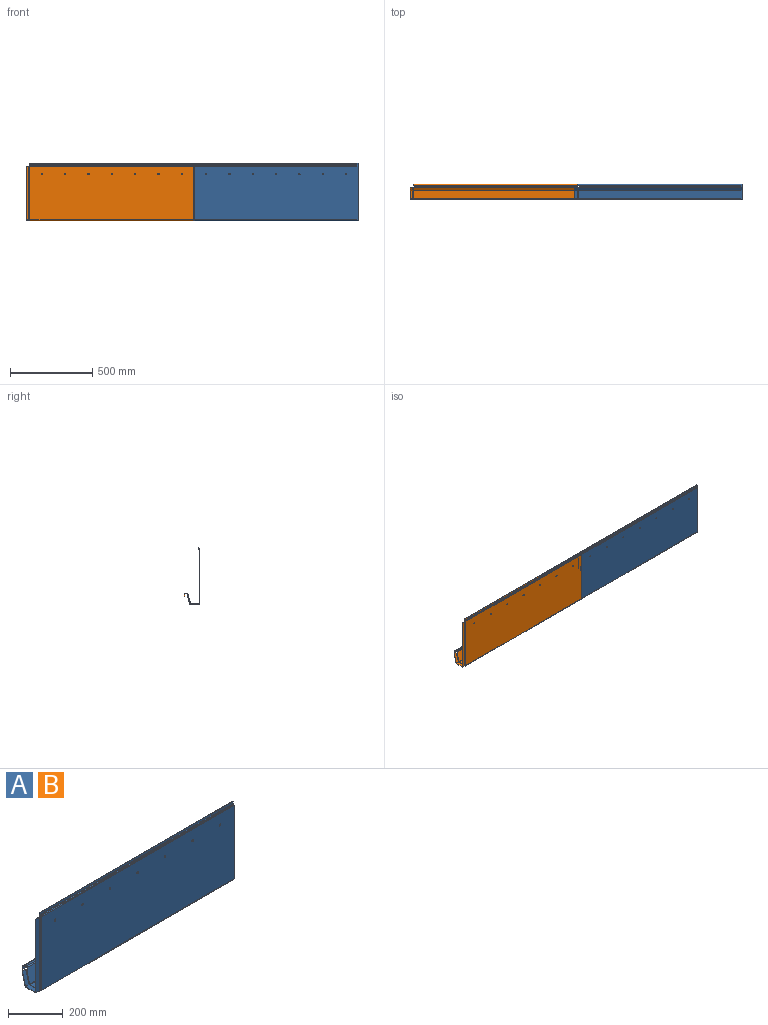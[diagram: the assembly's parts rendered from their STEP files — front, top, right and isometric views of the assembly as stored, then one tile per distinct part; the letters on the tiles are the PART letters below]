
ASSEMBLY  parts=2 mates=1
PART A: 122 faces, bbox 1022x95.1x350 mm
  f0: plane 327.93x2mm, normal (1,0,0), area 655.9mm2, adj f8,f9,f42,f51
  f1: cylinder r=4mm len=8mm, axis (0,1,0), area 50.3mm2, adj f8,f9
  f2: cylinder r=4mm len=8mm, axis (0,1,0), area 50.3mm2, adj f8,f9
  f3: cylinder r=4mm len=8mm, axis (0,1,0), area 50.3mm2, adj f8,f9
  f4: cylinder r=4mm len=8mm, axis (0,1,0), area 50.3mm2, adj f8,f9
  f5: cylinder r=4mm len=8mm, axis (0,1,0), area 50.3mm2, adj f8,f9
  f6: cylinder r=4mm len=8mm, axis (0,1,0), area 50.3mm2, adj f8,f9
  f7: cylinder r=4mm len=8mm, axis (0,1,0), area 50.3mm2, adj f8,f9
  f8: plane 997.93x327.93mm, normal (0,1,0), area 326897.8mm2, adj f0,f1,f2,f3,f4,f5,f6,f7
  f9: plane 997.93x327.93mm, normal (0,-1,0), area 326897.8mm2, adj f0,f1,f2,f3,f4,f5,f6,f7
  f10: cylinder r=2.5mm len=2mm, axis (0,-1,0), area 1.3mm2, adj f8,f9,f52,f91
  f11: plane 62.2x18.46mm, normal (1,0,0), area 127.7mm2, adj f12,f13,f16,f34
  f12: plane 997.93x61.69mm, normal (0,-0.97,0.26), area 63697.8mm2, adj f11,f14,f15,f18,f37,f115
  f13: plane 997.93x61.69mm, normal (0,0.97,-0.26), area 63697.8mm2, adj f11,f14,f15,f19,f36,f114
  f14: cylinder r=4.47mm len=2.36mm, axis (0,0.97,-0.26), area 5.5mm2, adj f12,f13,f35,f112
  f15: cylinder r=8.8mm len=6.89mm, axis (0,0.97,-0.26), area 19.4mm2, adj f12,f13,f17,f113
  f16: plane 4.83x4.22mm, normal (1,0,0), area 10.5mm2, adj f11,f18,f19,f21
  f17: bspline ~4.83x4.22mm, area 10.6mm2, adj f15,f18,f19,f24
  f18: cylinder r=5mm len=991.04mm, axis (1,0,0), area 6486.3mm2, adj f12,f16,f17,f22
  f19: cylinder r=3mm len=991.04mm, axis (1,0,0), area 3891.8mm2, adj f13,f16,f17,f23
  f20: plane 3.47x2mm, normal (-1,0,0), area 6.9mm2, adj f22,f23,f24,f26
  f21: plane 9.7x2mm, normal (1,0,0), area 19.4mm2, adj f16,f22,f23,f25
  f22: plane 1000x9.7mm, normal (0,0,1), area 9656mm2, adj f18,f20,f21,f24,f27
  f23: plane 1000x9.7mm, normal (0,0,-1), area 9656mm2, adj f19,f20,f21,f24,f28
  f24: cylinder r=8.8mm len=8.96mm, axis (0,0,-1), area 23.5mm2, adj f17,f20,f22,f23
  f25: plane 5x5mm, normal (1,0,0), area 12.6mm2, adj f21,f27,f28,f30
  f26: plane 5x5mm, normal (-1,0,0), area 12.6mm2, adj f20,f27,f28,f29
  f27: cylinder r=5mm len=1000mm, axis (1,0,0), area 7854mm2, adj f22,f25,f26,f32
  f28: cylinder r=3mm len=1000mm, axis (1,0,0), area 4712.4mm2, adj f23,f25,f26,f33
  f29: plane 12x2mm, normal (-1,0,0), area 24mm2, adj f26,f31,f32,f33
  f30: plane 12x2mm, normal (1,0,0), area 24mm2, adj f25,f31,f32,f33
  f31: plane 1000x2mm, normal (0,0,-1), area 2000mm2, adj f29,f30,f32,f33
  f32: plane 1000x12mm, normal (0,1,0), area 12000mm2, adj f27,f29,f30,f31
  f33: plane 1000x12mm, normal (0,-1,0), area 12000mm2, adj f28,f29,f30,f31
  f34: plane 4.83x4.22mm, normal (1,0,0), area 10.5mm2, adj f11,f36,f37,f38
  f35: bspline ~4.83x4.22mm, area 11.1mm2, adj f14,f36,f37,f41
  f36: cylinder r=5mm len=995.8mm, axis (1,0,0), area 6513.9mm2, adj f13,f34,f35,f40
  f37: cylinder r=3mm len=995.8mm, axis (1,0,0), area 3908.3mm2, adj f12,f34,f35,f39
  f38: plane 51.16x2mm, normal (1,0,0), area 102.3mm2, adj f34,f39,f40,f42
  f39: plane 997.93x51.16mm, normal (0,0,1), area 51055.3mm2, adj f37,f38,f41,f45,f83
  f40: plane 997.93x51.16mm, normal (0,0,-1), area 51055.3mm2, adj f36,f38,f41,f44,f82
  f41: cylinder r=4.47mm len=2.13mm, axis (0,0,-1), area 5.5mm2, adj f35,f39,f40,f81
  f42: plane 5x5mm, normal (1,0,0), area 12.6mm2, adj f0,f38,f44,f45
  f43: plane 5x5mm, normal (-1,0,0), area 12.6mm2, adj f44,f45,f80,f90
  f44: cylinder r=5mm len=997.93mm, axis (1,0,0), area 7837.7mm2, adj f9,f40,f42,f43
  f45: cylinder r=3mm len=997.93mm, axis (1,0,0), area 4702.6mm2, adj f8,f39,f42,f43
  f46: plane 3.43x3.43mm, normal (-1,0,0), area 5.7mm2, adj f48,f49,f50,f56
  f47: plane 4.07x4.07mm, normal (1,0,0), area 7.5mm2, adj f48,f49,f51,f55
  f48: plane 1000x2.66mm, normal (0,0.71,-0.71), area 3755.5mm2, adj f46,f47,f50,f54,f57
  f49: plane 1000x2.66mm, normal (0,-0.71,0.71), area 3755.5mm2, adj f46,f47,f50,f53,f58
  f50: cylinder r=2.5mm len=2.52mm, axis (0,-0.71,0.71), area 5.6mm2, adj f46,f48,f49,f52
  f51: plane 3.54x2.88mm, normal (1,0,0), area 6.3mm2, adj f0,f47,f53,f54
  f52: bspline ~3.54x2.88mm, area 6.7mm2, adj f10,f50,f53,f54
  f53: cylinder r=5mm len=997.48mm, axis (1,0,0), area 3915.7mm2, adj f9,f49,f51,f52
  f54: cylinder r=3mm len=997.48mm, axis (1,0,0), area 2349.4mm2, adj f8,f48,f51,f52
  f55: plane 3.54x2.88mm, normal (1,0,0), area 6.3mm2, adj f47,f57,f58,f61
  f56: plane 3.54x2.88mm, normal (-1,0,0), area 6.3mm2, adj f46,f57,f58,f59
  f57: cylinder r=5mm len=1000mm, axis (1,0,0), area 3927mm2, adj f48,f55,f56,f62
  f58: cylinder r=3mm len=1000mm, axis (1,0,0), area 2356.2mm2, adj f49,f55,f56,f63
  f59: plane 8.76x2mm, normal (-1,0,0), area 17.5mm2, adj f56,f60,f62,f63
  f60: plane 1000x2mm, normal (0,0,1), area 2000mm2, adj f59,f61,f62,f63
  f61: plane 8.76x2mm, normal (1,0,0), area 17.5mm2, adj f55,f60,f62,f63
  f62: plane 1000x8.76mm, normal (0,1,0), area 8757.4mm2, adj f57,f59,f60,f61
  f63: plane 1000x8.76mm, normal (0,-1,0), area 8757.4mm2, adj f58,f59,f60,f61
  f64: plane 2.04x1.41mm, normal (0.71,0,-0.71), area 4.1mm2, adj f66,f67,f68,f80
  f65: plane 1.48x1.41mm, normal (-0.71,0,0.71), area 3mm2, adj f66,f67,f68,f76
  f66: plane 1.9x1.9mm, normal (-0.41,-0.82,0.41), area 1.7mm2, adj f64,f65,f67,f68
  f67: plane 51.88x0.49mm, normal (0.71,0,0.71), area 35.3mm2, adj f64,f65,f66,f69,f78,f83
  f68: plane 51.88x0.49mm, normal (-0.71,0,-0.71), area 35.3mm2, adj f64,f65,f66,f69,f79,f82
  f69: cylinder r=4.47mm len=1.9mm, axis (-0.71,0,-0.71), area 1.5mm2, adj f67,f68,f77,f81
  f70: plane 17.93x2mm, normal (0,-1,0), area 35.9mm2, adj f72,f73,f74,f76
  f71: plane 17.93x2mm, normal (0,1,0), area 35.9mm2, adj f72,f73,f74,f75
  f72: plane 51.29x2mm, normal (-1,0,0), area 102.6mm2, adj f70,f71,f73,f74
  f73: plane 51.29x17.93mm, normal (0,0,1), area 919.5mm2, adj f70,f71,f72,f78
  f74: plane 51.29x17.93mm, normal (0,0,-1), area 919.5mm2, adj f70,f71,f72,f79
  f75: bspline ~3.54x2.88mm, area 6.8mm2, adj f71,f77,f78,f79
  f76: plane 3.54x2.88mm, normal (0,-1,0), area 6.3mm2, adj f65,f70,f78,f79
  f77: plane 2.51x1.41mm, normal (0.71,0,-0.71), area 5mm2, adj f69,f75,f78,f79
  f78: cylinder r=5mm len=52.42mm, axis (0,1,0), area 203.6mm2, adj f67,f73,f75,f76,f77
  f79: cylinder r=3mm len=52.42mm, axis (0,1,0), area 122.2mm2, adj f68,f74,f75,f76,f77
  f80: plane 3.54x2.88mm, normal (0,-1,0), area 6.3mm2, adj f43,f64,f82,f83
  f81: bspline ~3.54x2.88mm, area 6.4mm2, adj f41,f69,f82,f83
  f82: cylinder r=5mm len=49.52mm, axis (0,-1,0), area 194.5mm2, adj f40,f68,f80,f81
  f83: cylinder r=3mm len=49.52mm, axis (0,-1,0), area 116.7mm2, adj f39,f67,f80,f81
  f84: plane 2.04x1.41mm, normal (0.71,-0.71,0), area 4.1mm2, adj f86,f87,f88,f90
  f85: plane 1.59x1.59mm, normal (0,0,1), area 0.5mm2, adj f87,f88,f89,f95
  f86: plane 1.9x1.9mm, normal (-0.41,0.41,-0.82), area 1.7mm2, adj f84,f87,f88,f94
  f87: plane 329.97x0.49mm, normal (0.71,0.71,0), area 226.2mm2, adj f84,f85,f86,f89,f93,f96
  f88: plane 329.97x0.49mm, normal (-0.71,-0.71,0), area 226.2mm2, adj f84,f85,f86,f89,f92,f97
  f89: cylinder r=2.5mm len=1.73mm, axis (-0.71,-0.71,0), area 1.3mm2, adj f85,f87,f88,f91
  f90: plane 3.54x2.88mm, normal (0,0,-1), area 6.3mm2, adj f43,f84,f92,f93
  f91: bspline ~3.54x2.88mm, area 6.7mm2, adj f10,f89,f92,f93
  f92: cylinder r=5mm len=327.48mm, axis (0,0,1), area 1284.6mm2, adj f9,f88,f90,f91
  f93: cylinder r=3mm len=327.48mm, axis (0,0,1), area 770.8mm2, adj f8,f87,f90,f91
  f94: bspline ~3.54x2.88mm, area 7.1mm2, adj f86,f96,f97,f99
  f95: plane 3.54x2.88mm, normal (0,0,1), area 6.3mm2, adj f85,f96,f97,f98
  f96: cylinder r=5mm len=329.48mm, axis (0,0,-1), area 1291mm2, adj f87,f94,f95,f101
  f97: cylinder r=3mm len=329.48mm, axis (0,0,-1), area 774.6mm2, adj f88,f94,f95,f102
  f98: plane 17.93x2mm, normal (0,0,1), area 35.9mm2, adj f95,f100,f101,f102
  f99: plane 17.93x2mm, normal (0,0,-1), area 35.9mm2, adj f94,f100,f101,f102
  f100: plane 328x2mm, normal (-1,0,0), area 656mm2, adj f98,f99,f101,f102
  f101: plane 328x17.93mm, normal (0,1,0), area 5880.7mm2, adj f96,f98,f99,f100
  f102: plane 328x17.93mm, normal (0,-1,0), area 5880.7mm2, adj f97,f98,f99,f100
  f103: plane 54.65x15.07mm, normal (0.71,-0.68,0.18), area 38.7mm2, adj f105,f106,f110,f115
  f104: plane 54.65x15.07mm, normal (-0.71,0.68,-0.18), area 38.7mm2, adj f105,f106,f111,f114
  f105: cylinder r=8.8mm len=1.9mm, axis (-0.71,0.68,-0.18), area 1.4mm2, adj f103,f104,f109,f113
  f106: cylinder r=4.47mm len=1.92mm, axis (-0.71,0.68,-0.18), area 1.5mm2, adj f103,f104,f108,f112
  f107: bspline ~3.54x2.49mm, area 6.8mm2, adj f108,f110,f111,f117
  f108: plane 2.79x2.02mm, normal (0.71,0.68,-0.18), area 5mm2, adj f106,f107,f110,f111
  f109: bspline ~3.54x2.49mm, area 7mm2, adj f105,f110,f111,f121
  f110: cylinder r=5mm len=58.88mm, axis (0,0.26,0.97), area 232.7mm2, adj f103,f107,f108,f109,f119
  f111: cylinder r=3mm len=58.73mm, axis (0,0.26,0.97), area 139.6mm2, adj f104,f107,f108,f109,f120
  f112: bspline ~3.54x2.83mm, area 6.4mm2, adj f14,f106,f114,f115
  f113: bspline ~3.54x2.78mm, area 6.3mm2, adj f15,f105,f114,f115
  f114: cylinder r=5mm len=54.58mm, axis (0,-0.26,-0.97), area 220.3mm2, adj f13,f104,f112,f113
  f115: cylinder r=3mm len=54.42mm, axis (0,-0.26,-0.97), area 132.2mm2, adj f12,f103,f112,f113
  f116: plane 14.79x1.93mm, normal (0,0.26,0.97), area 29.6mm2, adj f118,f119,f120,f121
  f117: plane 17.93x1.93mm, normal (0,-0.26,-0.97), area 35.9mm2, adj f107,f118,f119,f120
  f118: plane 62.25x18.47mm, normal (-1,0,0), area 127.8mm2, adj f116,f117,f119,f120
  f119: plane 61.74x17.93mm, normal (0,-0.97,0.26), area 1137.3mm2, adj f110,f116,f117,f118,f121
  f120: plane 61.74x17.93mm, normal (0,0.97,-0.26), area 1137.3mm2, adj f111,f116,f117,f118,f121
  f121: cylinder r=8.8mm len=4.85mm, axis (0,0.97,-0.26), area 11.1mm2, adj f109,f116,f119,f120
PART B: same geometry as A
PLACE A t=(276.05,413.63,-155.6)mm
PLACE B t=(-723.95,413.63,-155.6)mm
MATE fastened B.f63 <-> A.f63  axis (0,-1,0) through (276.05,418.63,194.4)mm
